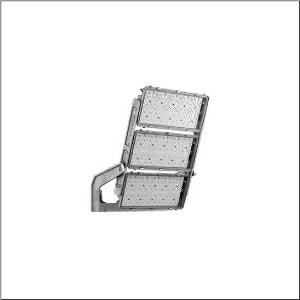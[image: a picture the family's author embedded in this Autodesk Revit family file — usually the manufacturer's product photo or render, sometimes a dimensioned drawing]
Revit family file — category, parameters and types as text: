
# Revit family: floodlight_fl_11_maxi_pro_remote___pl43_5xa779426a01aa_52e7
name_source: partatom
category: Lighting Fixtures
units: mm (PartAtom-declared; Revit-internal decimal feet)

## family parameters
Cut with Voids When Loaded = No
Host = Face
Light Source = No
Part Type = Normal
Room Calculation Point = No
Round Connector Dimension = Use Diameter
Shared = No

## types (1)
- --- (1 x LED, 172790 lm, 1387.6 W, 4000K)
    Apparent Load = 1388 VA
    CIE Flux Codes = 25 74 99 100 100
    Color Rendering = 70
    Color Temperature = 4000K
    Default Elevation = 1800 mm
    Description = Floodlight FL 11  maxi  pro Remote floodlight; light control with lens of PMMA; cover panel of toughened safety glass, transparent; light distribution: PL43, asymmetric direct distribution, LEDcolour temperature: 4000K, rated luminous flux: 172.790lm, colour rendering: CRI > 70, light colour: 740; luminous efficacy: 125lm/W; brightness control: DALI 2 (1 DALI address); with terminal, 8-pole, max. 2.5mm², mains connection: 220..240V/380..400V AC, 50/60Hz, surge voltage resistance: line to ground: 10kV, ECG replaceable separately, LED unit replaceable without ESD environment, dustproof LED module, dimming range 10..100%, no afterglow with DALI off / DMX off command; 1388W floodlight with 2x LED unit of diecast aluminium, coated grey; length: 713mm / width: 651mm / height: 338mm; mounting bracket, of diecast aluminium, uncoated, natural, equipment: Power, protection rating (complete): IP66; insulation class (complete): insulation class I (protective earthing); certification: CE, ENEC, VDE; ball protection: ball impact resistance with accessories, impact resistance: IK07; rated ambient temperature 10°C, only for outdoor installations, permissible operating ambient temperature: -40..+30°C, permissible storage temperature: -40..+85°Cpackaging unit: 1 piece

Light Distribution: PL43
    Height = 320 mm
    Lamp = 1 x LED
    Lamp Light Flux = 172790 lm
    Lamp Power = 1387.6 W
    Lamp count = 1
    Length = 1002 mm
    Luminous efficacy = 125 lm/W
    Manufacturer = Siteco
    ModVariant = No
    Model = 5XA779426A01AA
    Mounting Place = Ceiling
    Mounting Type = Surface mounted
    Number of Poles = 1
    OnlyDefault = Yes
    Power Factor = 1
    Product Name = Floodlight FL 11 maxi pro Remote | PL43
    Product group = floodlight | ceiling mounted
    ProductGroupID = 301
    Protection Class = Protection class I
    Protection Degree = IP 66
    RLX_Detail_Level = 1
    RLX_Emergency_Light_Flux = 0 lm
    RLX_Emergency_Type = 0
    RLX_Emergency_Type_DB = No
    RlxData = <blob elided: 52617 chars, md5=030798f1>
    Socket = socket
    Standby Power = 0 W
    System Light Flux = 172790 lm
    System Power = 1388 W
    Type Comments = factory setting: luminous flux: 100 % | dim-lin: 254 | 955 mA
    Type Image = l_1349141.jpg
    URL = http://relux.com
    VarID = @adj_096386
    Voltage = 0 V
    Weight = 0.00 kg
    Width = 655 mm

## geometry (parser evidence)
native form markers: Blend x4, Sweep x15
no freeform markers — native parametric forms only
